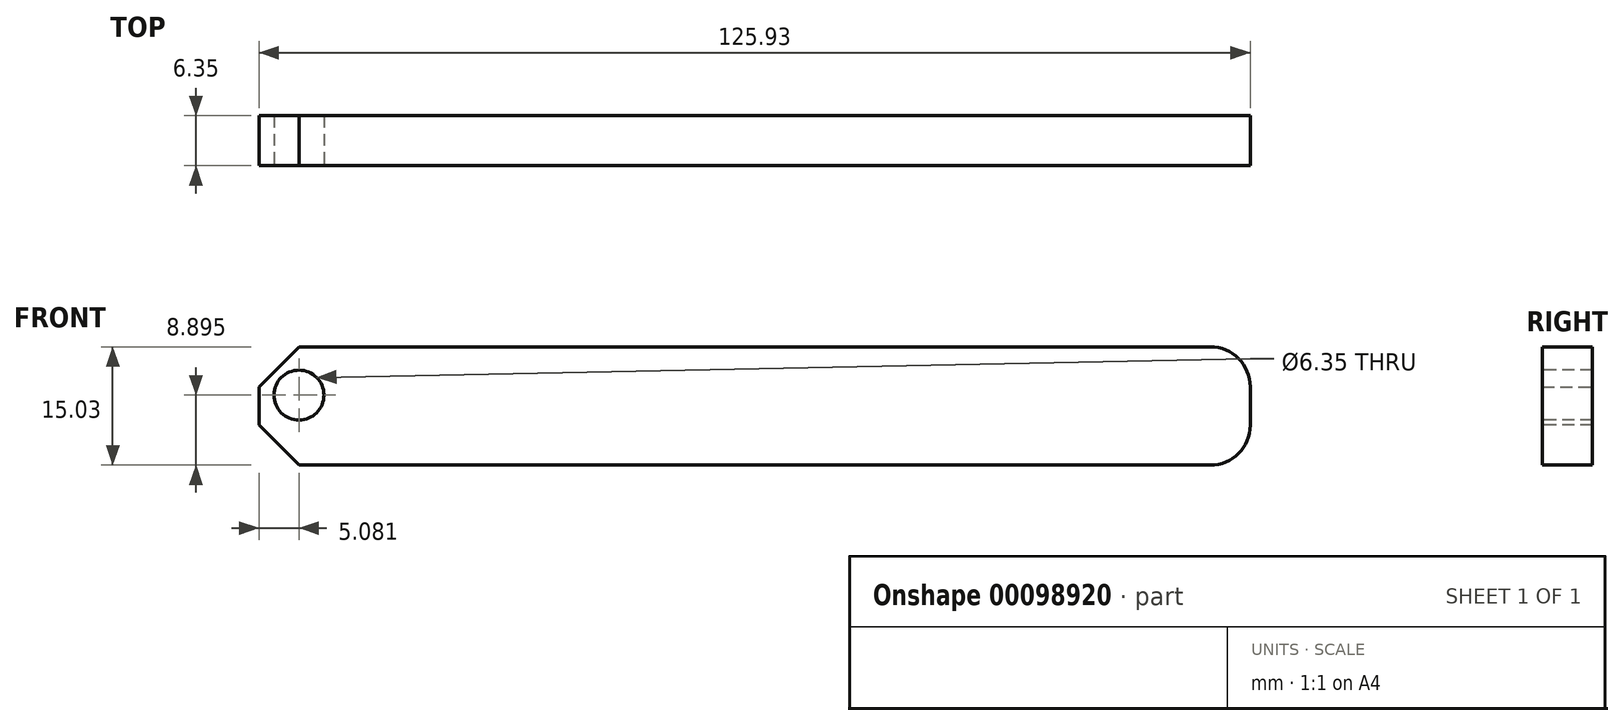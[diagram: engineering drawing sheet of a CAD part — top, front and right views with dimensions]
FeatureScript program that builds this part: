
annotation { "Feature Type Name" : "Feature", "Feature Type Description" : "" }
export const myFeature = defineFeature(function(context is Context, id is Id, definition is map)
    precondition{}
    {
        {
            var Q0;
            Q0=qCreatedBy(makeId("Front.planeOp"),FACE);
            var sketch = newSketch(context, id + "F0", { "sketchPlane" : qUnion([Q0])});
            skLineSegment(sketch, "E0.bottom", {"start": v(-47.75, 28.03) * mm, "end": v(78.18, 28.03) * mm});
            skLineSegment(sketch, "E0.top", {"start": v(-47.75, 13) * mm, "end": v(78.18, 13) * mm});
            skLineSegment(sketch, "E0.left", {"start": v(-47.75, 28.03) * mm, "end": v(-47.75, 13) * mm});
            skLineSegment(sketch, "E0.right", {"start": v(78.18, 28.03) * mm, "end": v(78.18, 13) * mm});
            skSolve(sketch);
        }
        {
            var Q0;
            Q0 = qSketchRegion(id + "F0", true);
            extrude(context, id + "F1", {"entities" : qUnion([Q0]), "depth" : 6.35 * mm});
        }
        {
            var Q0;
            Q0=makeQuery(id+"F1.opExtrude","SWEPT_EDGE",EDGE,{"disambiguationData":[OSD([sQuery(id+"F0.wireOp",EDGE,"E0.bottom"),sQuery(id+"F0.wireOp",EDGE,"E0.right")])]});
            var Q1;
            Q1=makeQuery(id+"F1.opExtrude","SWEPT_EDGE",EDGE,{"disambiguationData":[OSD([sQuery(id+"F0.wireOp",EDGE,"E0.top"),sQuery(id+"F0.wireOp",EDGE,"E0.right")])]});
            fillet(context, id + "F2", {"entities" : qUnion([Q0, Q1]), "radius" : 5.08 * mm, "tangentPropagation" : true, "allowEdgeOverflow" : false});
        }
        {
            var Q0;
            Q0=makeQuery(id+"F1.opExtrude","SWEPT_EDGE",EDGE,{"disambiguationData":[OSD([sQuery(id+"F0.wireOp",EDGE,"E0.bottom"),sQuery(id+"F0.wireOp",EDGE,"E0.left")])]});
            var Q1;
            Q1=makeQuery(id+"F1.opExtrude","SWEPT_EDGE",EDGE,{"disambiguationData":[OSD([sQuery(id+"F0.wireOp",EDGE,"E0.top"),sQuery(id+"F0.wireOp",EDGE,"E0.left")])]});
            chamfer(context, id + "F3", {"entities" : qUnion([Q0, Q1]), "width" : 5.08 * mm, "tangentPropagation" : true});
        }
        {
            var Q0;
            Q0=makeQuery(id+"F1.opExtrude","CAP_FACE",FACE,{"disambiguationData":[OSD([sQuery(id+"F0.wireOp",EDGE,"E0.bottom"),sQuery(id+"F0.wireOp",EDGE,"E0.top"),sQuery(id+"F0.wireOp",EDGE,"E0.left"),sQuery(id+"F0.wireOp",EDGE,"E0.right")])],"isStart":false});
            var sketch = newSketch(context, id + "F4", { "sketchPlane" : qUnion([Q0])});
            skPoint(sketch, "E1", {"position": v(-42.67, 21.9) * mm});
            skSolve(sketch);
        }
        {
            var Q0;
            Q0=sQuery(id+"F4.wireOp",VERTEX,"E1");
            var Q1;
            Q1=makeQuery(id+"F1.opExtrude","SWEPT_BODY",BODY,{"disambiguationData":[OSD([sQuery(id+"F0.wireOp",EDGE,"E0.bottom"),sQuery(id+"F0.wireOp",EDGE,"E0.top"),sQuery(id+"F0.wireOp",EDGE,"E0.left"),sQuery(id+"F0.wireOp",EDGE,"E0.right")])]});
            hole(context, id + "F5", {"style" : HoleStyle.SIMPLE, "endStyle" : HoleEndStyle.THROUGH, "holeDiameter" : 6.35 * mm, "locations" : qUnion([Q0]), "scope" : qUnion([Q1]), "isTappedThrough" : true});
        }
    });
